# Revit family: Heater-Bromic-Tungsten-Gas-Portable_AU_23
name_source: partatom
category: Mechanical Equipment
units: mm (PartAtom-declared; Revit-internal decimal feet)

## family parameters
Always vertical = No
Classification = None
Cut with Voids When Loaded = No
OmniClass Number = 23.75.10.17.14.14
OmniClass Title = Fuel-Fired Radiant Heaters
Part Type = Normal
Room Calculation Point = No
Round Connector Dimension = Use Diameter
Shared = No
Work Plane-Based = Yes

## types (1)
- Tungsten Gas - LPG - Portable
    Approximate Heat Area = 20.00 m²
    Default Elevation = 0 mm  [stored 0 ft]
    Depth = 686 mm
    Description = The award-winning Bromic Tungsten Smart-Heat™ Portable heater offers efficient heating in a stylish, modular, and maneuverable design with a neutral black finish.
    Heater Material = Metal-Steel-Bromic-Black-Perforated
    Height = 2159 mm
    LPG = Yes
    Manufacturer = Bromic Heating
    Material = Metal-Steel-Bromic-Black
    Model = Tungsten Smart-Heat™ Gas Portable
    Mount Material = Metal-Steel-Bromic-Black
    Product data url = https://www.bimobject.com
    ProductCode = 2620350-1
    Screen Material = Metal-Steel-Bromic-Black
    URL = https://www.bromic.com.au
    Weight = 56.0 kg
    Width = 483 mm

note: [stored X ft] marks values corroborated as IEEE doubles in the binary element streams (Revit-internal decimal feet)

## geometry (parser evidence)
native form markers: Sweep x2
no freeform markers — native parametric forms only
